# Revit family: Hitachi_RPIW-M-4-Pipes_LOD400
name_source: partatom
category: Mechanical Equipment
revit_build: Autodesk Revit 2018 (Build: 20181015_0930(x64)
units: mm (PartAtom-declared; Revit-internal decimal feet)

## family parameters
Always vertical = Yes
Cut with Voids When Loaded = No
Part Type = Normal
Room Calculation Point = Yes
Round Connector Dimension = Use Diameter
Shared = No
Work Plane-Based = No

## types (7) — shared parameters
Cooling Water Flow = 0.0 L/s
Description = Fan Coil Unit - RPIW-M
Manufacturer = Hitachi Air Conditioning Europe SAS
Model = RPIW-M
Phase = 1
Pipe Diam. = 1/2"
Product Line = RPIW-M
Service Space = 500 mm  [stored 1.64042 ft]
Voltage = 230 V
Waste Water = 15 mm  [stored 0.0492126 ft]
data = CRSLeCRSLECM_R0
hook = 13 mm  [stored 0.0426509 ft]

## type names (no varying parameters)
- RPIW 734-M
- RPIW 634-M
- RPIW 534-M
- RPIW 434-M
- RPIW 334-M
- RPIW 234-M
- RPIW 134-M

note: [stored X ft] marks values corroborated as IEEE doubles in the binary element streams (Revit-internal decimal feet)
